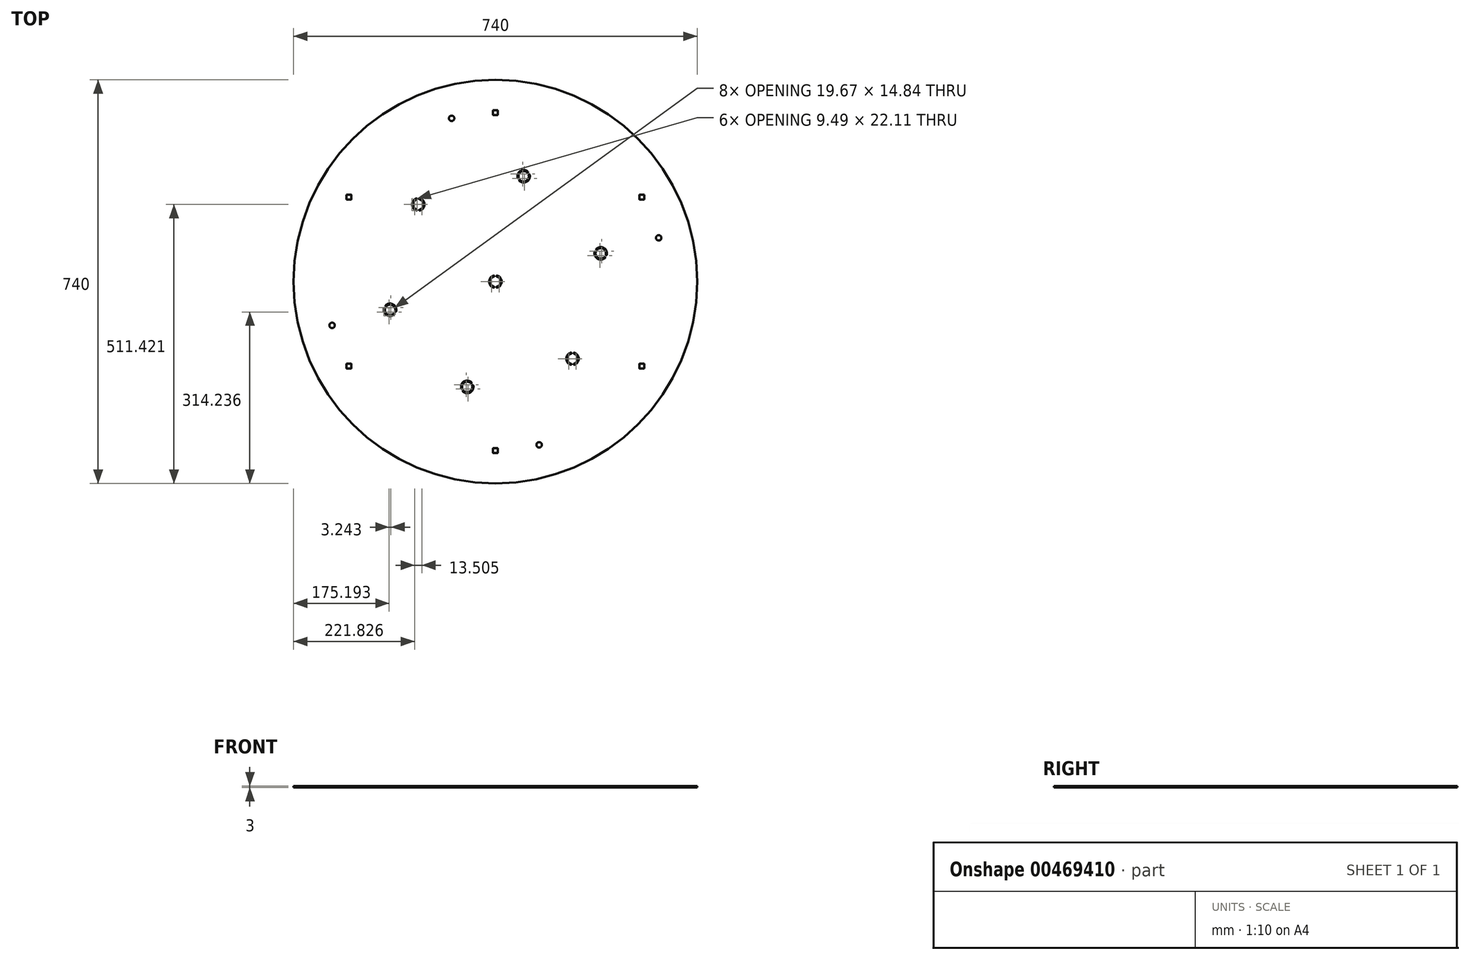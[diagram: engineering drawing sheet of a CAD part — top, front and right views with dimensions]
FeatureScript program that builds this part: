
annotation { "Feature Type Name" : "Feature", "Feature Type Description" : "" }
export const myFeature = defineFeature(function(context is Context, id is Id, definition is map)
    precondition{}
    {
        {
            var Q0;
            Q0=qCreatedBy(makeId("Top.planeOp"),FACE);
            var sketch = newSketch(context, id + "F0", { "sketchPlane" : qUnion([Q0])});
            skCircle(sketch, "E0", {"center": v(0, 0) * mm, "radius": 370 * mm});
            skSolve(sketch);
        }
        {
            var Q0;
            Q0=makeQuery(id+"F0.imprint","IMPRINT",FACE,{"disambiguationData":[TD([[makeQuery(id+"F0.imprint","IMPRINT",EDGE,{"derivedFrom":sQuery(id+"F0.wireOp",EDGE,"E0")}),1.0]])]});
            extrude(context, id + "F1", {"entities" : qUnion([Q0]), "depth" : 3 * mm});
        }
        {
            var Q0;
            Q0=makeQuery(id+"F1.opExtrude","CAP_FACE",FACE,{"disambiguationData":[OSD([sQuery(id+"F0.wireOp",EDGE,"E0")])],"isStart":false});
            var sketch = newSketch(context, id + "F2", { "sketchPlane" : qUnion([Q0])});
            skLineSegment(sketch, "E1", {"start": v(0, 310) * mm, "end": v(268.47, 155) * mm, "construction": true});
            skLineSegment(sketch, "E2", {"start": v(268.47, 155) * mm, "end": v(268.47, -155) * mm, "construction": true});
            skLineSegment(sketch, "E3", {"start": v(268.47, -155) * mm, "end": v(0, -310) * mm, "construction": true});
            skLineSegment(sketch, "E4", {"start": v(0, -310) * mm, "end": v(-268.47, -155) * mm, "construction": true});
            skLineSegment(sketch, "E5", {"start": v(-268.47, -155) * mm, "end": v(-268.47, 155) * mm, "construction": true});
            skLineSegment(sketch, "E6", {"start": v(-268.47, 155) * mm, "end": v(0, 310) * mm, "construction": true});
            skLineSegment(sketch, "E7.bottom", {"start": v(4, 314.5) * mm, "end": v(-4, 314.5) * mm});
            skLineSegment(sketch, "E7.top", {"start": v(4, 305.5) * mm, "end": v(-4, 305.5) * mm});
            skLineSegment(sketch, "E7.left", {"start": v(4.5, 314) * mm, "end": v(4.5, 306) * mm});
            skLineSegment(sketch, "E7.right", {"start": v(-4.5, 314) * mm, "end": v(-4.5, 306) * mm});
            skPoint(sketch, "E7.middle", {"position": v(0, 310) * mm});
            skLineSegment(sketch, "E8.bottom", {"start": v(272.47, 159.5) * mm, "end": v(264.47, 159.5) * mm});
            skLineSegment(sketch, "E8.top", {"start": v(272.47, 150.5) * mm, "end": v(264.47, 150.5) * mm});
            skLineSegment(sketch, "E8.left", {"start": v(272.97, 159) * mm, "end": v(272.97, 151) * mm});
            skLineSegment(sketch, "E8.right", {"start": v(263.97, 159) * mm, "end": v(263.97, 151) * mm});
            skPoint(sketch, "E8.middle", {"position": v(268.47, 155) * mm});
            skLineSegment(sketch, "E9.bottom", {"start": v(272.47, -150.5) * mm, "end": v(264.47, -150.5) * mm});
            skLineSegment(sketch, "E9.top", {"start": v(272.47, -159.5) * mm, "end": v(264.47, -159.5) * mm});
            skLineSegment(sketch, "E9.left", {"start": v(272.97, -151) * mm, "end": v(272.97, -159) * mm});
            skLineSegment(sketch, "E9.right", {"start": v(263.97, -151) * mm, "end": v(263.97, -159) * mm});
            skPoint(sketch, "E9.middle", {"position": v(268.47, -155) * mm});
            skLineSegment(sketch, "E10.bottom", {"start": v(-4, -305.5) * mm, "end": v(4, -305.5) * mm});
            skLineSegment(sketch, "E10.top", {"start": v(-4, -314.5) * mm, "end": v(4, -314.5) * mm});
            skLineSegment(sketch, "E10.left", {"start": v(-4.5, -306) * mm, "end": v(-4.5, -314) * mm});
            skLineSegment(sketch, "E10.right", {"start": v(4.5, -306) * mm, "end": v(4.5, -314) * mm});
            skPoint(sketch, "E10.middle", {"position": v(0, -310) * mm});
            skLineSegment(sketch, "E11.bottom", {"start": v(-264.47, -150.5) * mm, "end": v(-272.47, -150.5) * mm});
            skLineSegment(sketch, "E11.top", {"start": v(-264.47, -159.5) * mm, "end": v(-272.47, -159.5) * mm});
            skLineSegment(sketch, "E11.left", {"start": v(-263.97, -151) * mm, "end": v(-263.97, -159) * mm});
            skLineSegment(sketch, "E11.right", {"start": v(-272.97, -151) * mm, "end": v(-272.97, -159) * mm});
            skPoint(sketch, "E11.middle", {"position": v(-268.47, -155) * mm});
            skLineSegment(sketch, "E12.bottom", {"start": v(-264.47, 150.5) * mm, "end": v(-272.47, 150.5) * mm});
            skLineSegment(sketch, "E12.top", {"start": v(-264.47, 159.5) * mm, "end": v(-272.47, 159.5) * mm});
            skLineSegment(sketch, "E12.left", {"start": v(-263.97, 151) * mm, "end": v(-263.97, 159) * mm});
            skLineSegment(sketch, "E12.right", {"start": v(-272.97, 151) * mm, "end": v(-272.97, 159) * mm});
            skPoint(sketch, "E12.middle", {"position": v(-268.47, 155) * mm});
            skPoint(sketch, "E13.visualSharp", {"position": v(-4.5, 314.5) * mm});
            skArc(sketch, "E13.filletArc", {"start": v(-4, 314.5) * mm, "mid": v(-4.35, 314.35) * mm, "end": v(-4.5, 314) * mm});
            skPoint(sketch, "E14.visualSharp", {"position": v(4.5, 314.5) * mm});
            skArc(sketch, "E14.filletArc", {"start": v(4.5, 314) * mm, "mid": v(4.35, 314.35) * mm, "end": v(4, 314.5) * mm});
            skPoint(sketch, "E15.visualSharp", {"position": v(4.5, 305.5) * mm});
            skArc(sketch, "E15.filletArc", {"start": v(4, 305.5) * mm, "mid": v(4.35, 305.65) * mm, "end": v(4.5, 306) * mm});
            skPoint(sketch, "E16.visualSharp", {"position": v(-4.5, 305.5) * mm});
            skArc(sketch, "E16.filletArc", {"start": v(-4.5, 306) * mm, "mid": v(-4.35, 305.65) * mm, "end": v(-4, 305.5) * mm});
            skPoint(sketch, "E17.visualSharp", {"position": v(263.97, 159.5) * mm});
            skArc(sketch, "E17.filletArc", {"start": v(264.47, 159.5) * mm, "mid": v(264.11, 159.35) * mm, "end": v(263.97, 159) * mm});
            skPoint(sketch, "E18.visualSharp", {"position": v(272.97, 159.5) * mm});
            skArc(sketch, "E18.filletArc", {"start": v(272.97, 159) * mm, "mid": v(272.82, 159.35) * mm, "end": v(272.47, 159.5) * mm});
            skPoint(sketch, "E19.visualSharp", {"position": v(272.97, 150.5) * mm});
            skArc(sketch, "E19.filletArc", {"start": v(272.47, 150.5) * mm, "mid": v(272.82, 150.65) * mm, "end": v(272.97, 151) * mm});
            skPoint(sketch, "E20.visualSharp", {"position": v(263.97, 150.5) * mm});
            skArc(sketch, "E20.filletArc", {"start": v(263.97, 151) * mm, "mid": v(264.11, 150.65) * mm, "end": v(264.47, 150.5) * mm});
            skPoint(sketch, "E21.visualSharp", {"position": v(263.97, -150.5) * mm});
            skArc(sketch, "E21.filletArc", {"start": v(264.47, -150.5) * mm, "mid": v(264.11, -150.65) * mm, "end": v(263.97, -151) * mm});
            skPoint(sketch, "E22.visualSharp", {"position": v(272.97, -150.5) * mm});
            skArc(sketch, "E22.filletArc", {"start": v(272.97, -151) * mm, "mid": v(272.82, -150.65) * mm, "end": v(272.47, -150.5) * mm});
            skPoint(sketch, "E23.visualSharp", {"position": v(272.97, -159.5) * mm});
            skArc(sketch, "E23.filletArc", {"start": v(272.47, -159.5) * mm, "mid": v(272.82, -159.35) * mm, "end": v(272.97, -159) * mm});
            skPoint(sketch, "E24.visualSharp", {"position": v(263.97, -159.5) * mm});
            skArc(sketch, "E24.filletArc", {"start": v(263.97, -159) * mm, "mid": v(264.11, -159.35) * mm, "end": v(264.47, -159.5) * mm});
            skPoint(sketch, "E25.visualSharp", {"position": v(-4.5, -305.5) * mm});
            skArc(sketch, "E25.filletArc", {"start": v(-4, -305.5) * mm, "mid": v(-4.35, -305.65) * mm, "end": v(-4.5, -306) * mm});
            skPoint(sketch, "E26.visualSharp", {"position": v(4.5, -305.5) * mm});
            skArc(sketch, "E26.filletArc", {"start": v(4.5, -306) * mm, "mid": v(4.35, -305.65) * mm, "end": v(4, -305.5) * mm});
            skPoint(sketch, "E27.visualSharp", {"position": v(4.5, -314.5) * mm});
            skArc(sketch, "E27.filletArc", {"start": v(4, -314.5) * mm, "mid": v(4.35, -314.35) * mm, "end": v(4.5, -314) * mm});
            skPoint(sketch, "E28.visualSharp", {"position": v(-4.5, -314.5) * mm});
            skArc(sketch, "E28.filletArc", {"start": v(-4.5, -314) * mm, "mid": v(-4.35, -314.35) * mm, "end": v(-4, -314.5) * mm});
            skPoint(sketch, "E29.visualSharp", {"position": v(-272.97, -159.5) * mm});
            skArc(sketch, "E29.filletArc", {"start": v(-272.97, -159) * mm, "mid": v(-272.82, -159.35) * mm, "end": v(-272.47, -159.5) * mm});
            skPoint(sketch, "E30.visualSharp", {"position": v(-272.97, -150.5) * mm});
            skArc(sketch, "E30.filletArc", {"start": v(-272.47, -150.5) * mm, "mid": v(-272.82, -150.65) * mm, "end": v(-272.97, -151) * mm});
            skPoint(sketch, "E31.visualSharp", {"position": v(-263.97, -150.5) * mm});
            skArc(sketch, "E31.filletArc", {"start": v(-263.97, -151) * mm, "mid": v(-264.11, -150.65) * mm, "end": v(-264.47, -150.5) * mm});
            skPoint(sketch, "E32.visualSharp", {"position": v(-263.97, -159.5) * mm});
            skArc(sketch, "E32.filletArc", {"start": v(-264.47, -159.5) * mm, "mid": v(-264.11, -159.35) * mm, "end": v(-263.97, -159) * mm});
            skPoint(sketch, "E33.visualSharp", {"position": v(-263.97, 150.5) * mm});
            skArc(sketch, "E33.filletArc", {"start": v(-264.47, 150.5) * mm, "mid": v(-264.11, 150.65) * mm, "end": v(-263.97, 151) * mm});
            skPoint(sketch, "E34.visualSharp", {"position": v(-263.97, 159.5) * mm});
            skArc(sketch, "E34.filletArc", {"start": v(-263.97, 159) * mm, "mid": v(-264.11, 159.35) * mm, "end": v(-264.47, 159.5) * mm});
            skPoint(sketch, "E35.visualSharp", {"position": v(-272.97, 159.5) * mm});
            skArc(sketch, "E35.filletArc", {"start": v(-272.47, 159.5) * mm, "mid": v(-272.82, 159.35) * mm, "end": v(-272.97, 159) * mm});
            skPoint(sketch, "E36.visualSharp", {"position": v(-272.97, 150.5) * mm});
            skArc(sketch, "E36.filletArc", {"start": v(-272.97, 151) * mm, "mid": v(-272.82, 150.65) * mm, "end": v(-272.47, 150.5) * mm});
            skSolve(sketch);
        }
        {
            var Q0;
            Q0 = qSketchRegion(id + "F2", true);
            extrude(context, id + "F3", {"entities" : qUnion([Q0]), "operationType" : NewBodyOperationType.REMOVE, "oppositeDirection" : true, "depth" : 5 * mm});
        }
        {
            var Q0;
            Q0=makeQuery(id+"F1.opExtrude","CAP_FACE",FACE,{"disambiguationData":[OSD([sQuery(id+"F0.wireOp",EDGE,"E0")])],"isStart":false});
            var sketch = newSketch(context, id + "F4", { "sketchPlane" : qUnion([Q0])});
            skArc(sketch, "E37", {"start": v(3.29, -11.02) * mm, "mid": v(11.5, 0) * mm, "end": v(3.29, 11.02) * mm});
            skArc(sketch, "E38", {"start": v(2.71, -9.1) * mm, "mid": v(9.5, 0) * mm, "end": v(2.71, 9.1) * mm});
            skLineSegment(sketch, "E39.left", {"start": v(-2, -10.06) * mm, "end": v(-2, -10.06) * mm});
            skLineSegment(sketch, "E39.right", {"start": v(2, -10.06) * mm, "end": v(2, -10.06) * mm});
            skLineSegment(sketch, "E40.trimOffspring", {"start": v(2, 10.06) * mm, "end": v(2, 10.06) * mm});
            skLineSegment(sketch, "E41.trimOffspring", {"start": v(-2, 10.06) * mm, "end": v(-2, 10.06) * mm});
            skArc(sketch, "E42.trimOffspring", {"start": v(-2.71, 9.1) * mm, "mid": v(-9.5, 0) * mm, "end": v(-2.71, -9.1) * mm});
            skArc(sketch, "E43.trimOffspring", {"start": v(-3.29, 11.02) * mm, "mid": v(-11.5, 0) * mm, "end": v(-3.29, -11.02) * mm});
            skPoint(sketch, "E44.visualSharp", {"position": v(-2, -11.32) * mm});
            skArc(sketch, "E44.filletArc", {"start": v(-3.29, -11.02) * mm, "mid": v(-2.4, -10.86) * mm, "end": v(-2, -10.06) * mm});
            skPoint(sketch, "E45.visualSharp", {"position": v(-2, -9.29) * mm});
            skArc(sketch, "E45.filletArc", {"start": v(-2, -10.06) * mm, "mid": v(-2.2, -9.46) * mm, "end": v(-2.71, -9.1) * mm});
            skPoint(sketch, "E46.visualSharp", {"position": v(2, -9.29) * mm});
            skArc(sketch, "E46.filletArc", {"start": v(2.71, -9.1) * mm, "mid": v(2.2, -9.46) * mm, "end": v(2, -10.06) * mm});
            skPoint(sketch, "E47.visualSharp", {"position": v(2, -11.32) * mm});
            skArc(sketch, "E47.filletArc", {"start": v(2, -10.06) * mm, "mid": v(2.4, -10.86) * mm, "end": v(3.29, -11.02) * mm});
            skPoint(sketch, "E48.visualSharp", {"position": v(-2, 9.29) * mm});
            skArc(sketch, "E48.filletArc", {"start": v(-2.71, 9.1) * mm, "mid": v(-2.2, 9.46) * mm, "end": v(-2, 10.06) * mm});
            skPoint(sketch, "E49.visualSharp", {"position": v(-2, 11.32) * mm});
            skArc(sketch, "E49.filletArc", {"start": v(-2, 10.06) * mm, "mid": v(-2.4, 10.86) * mm, "end": v(-3.29, 11.02) * mm});
            skPoint(sketch, "E50.visualSharp", {"position": v(2, 9.29) * mm});
            skArc(sketch, "E50.filletArc", {"start": v(2, 10.06) * mm, "mid": v(2.2, 9.46) * mm, "end": v(2.71, 9.1) * mm});
            skPoint(sketch, "E51.visualSharp", {"position": v(2, 11.32) * mm});
            skArc(sketch, "E51.filletArc", {"start": v(3.29, 11.02) * mm, "mid": v(2.4, 10.86) * mm, "end": v(2, 10.06) * mm});
            skSolve(sketch);
        }
        {
            var Q0;
            Q0=makeQuery(id+"F4.imprint","IMPRINT",FACE,{"disambiguationData":[TD([[makeQuery(id+"F4.imprint","IMPRINT",EDGE,{"derivedFrom":sQuery(id+"F4.wireOp",EDGE,"E37")}),-1.0]])]});
            extrude(context, id + "F5", {"entities" : qUnion([Q0]), "operationType" : NewBodyOperationType.INTERSECT, "endBound" : BoundingType.UP_TO_NEXT, "oppositeDirection" : true, "depth" : 3 * mm});
        }
        {
            var Q0;
            Q0=makeQuery(id+"F1.opExtrude","CAP_FACE",FACE,{"disambiguationData":[OSD([sQuery(id+"F0.wireOp",EDGE,"E0")])],"isStart":false});
            var sketch = newSketch(context, id + "F6", { "sketchPlane" : qUnion([Q0])});
            skLineSegment(sketch, "E52", {"start": v(80.23, -299.44) * mm, "end": v(-299.44, -80.23) * mm, "construction": true});
            skLineSegment(sketch, "E53", {"start": v(-299.44, -80.23) * mm, "end": v(-80.23, 299.44) * mm, "construction": true});
            skLineSegment(sketch, "E54", {"start": v(-80.23, 299.44) * mm, "end": v(299.44, 80.23) * mm, "construction": true});
            skLineSegment(sketch, "E55", {"start": v(299.44, 80.23) * mm, "end": v(80.23, -299.44) * mm, "construction": true});
            skLineSegment(sketch, "E56", {"start": v(-299.44, -80.23) * mm, "end": v(299.44, 80.23) * mm, "construction": true});
            skLineSegment(sketch, "E57", {"start": v(-80.23, 299.44) * mm, "end": v(80.23, -299.44) * mm, "construction": true});
            skCircle(sketch, "E58", {"center": v(-80.23, 299.44) * mm, "radius": 5 * mm});
            skCircle(sketch, "E59", {"center": v(299.44, 80.23) * mm, "radius": 5 * mm});
            skCircle(sketch, "E60", {"center": v(80.23, -299.44) * mm, "radius": 5 * mm});
            skCircle(sketch, "E61", {"center": v(-299.44, -80.23) * mm, "radius": 5 * mm});
            skSolve(sketch);
        }
        {
            var Q0;
            Q0=makeQuery(id+"F6.imprint","IMPRINT",FACE,{"disambiguationData":[TD([[makeQuery(id+"F6.imprint","IMPRINT",EDGE,{"derivedFrom":sQuery(id+"F6.wireOp",EDGE,"E58")}),-1.0]])]});
            extrude(context, id + "F7", {"entities" : qUnion([Q0]), "operationType" : NewBodyOperationType.INTERSECT, "oppositeDirection" : true, "depth" : 3 * mm});
        }
        {
            var Q0;
            Q0=makeQuery(id+"F1.opExtrude","CAP_FACE",FACE,{"disambiguationData":[OSD([sQuery(id+"F0.wireOp",EDGE,"E0")])],"isStart":false});
            var sketch = newSketch(context, id + "F8", { "sketchPlane" : qUnion([Q0])});
            skArc(sketch, "E62", {"start": v(-138.14, 130.4) * mm, "mid": v(-129.92, 141.42) * mm, "end": v(-138.14, 152.44) * mm});
            skArc(sketch, "E63", {"start": v(-138.7, 132.32) * mm, "mid": v(-131.92, 141.42) * mm, "end": v(-138.7, 150.53) * mm});
            skLineSegment(sketch, "E64.left", {"start": v(-143.42, 151.48) * mm, "end": v(-143.42, 151.48) * mm});
            skLineSegment(sketch, "E64.right", {"start": v(-139.42, 151.48) * mm, "end": v(-139.42, 151.48) * mm});
            skLineSegment(sketch, "E65.trimOffspring", {"start": v(-139.42, 131.36) * mm, "end": v(-139.42, 131.36) * mm});
            skLineSegment(sketch, "E66.trimOffspring", {"start": v(-143.42, 131.36) * mm, "end": v(-143.42, 131.36) * mm});
            skArc(sketch, "E67.trimOffspring", {"start": v(-144.14, 150.53) * mm, "mid": v(-150.92, 141.42) * mm, "end": v(-144.14, 132.32) * mm});
            skArc(sketch, "E68.trimOffspring", {"start": v(-144.7, 152.44) * mm, "mid": v(-152.92, 141.42) * mm, "end": v(-144.7, 130.4) * mm});
            skPoint(sketch, "E69.visualSharp", {"position": v(-143.42, 150.7) * mm});
            skArc(sketch, "E69.filletArc", {"start": v(-144.14, 150.53) * mm, "mid": v(-143.62, 150.89) * mm, "end": v(-143.42, 151.48) * mm});
            skPoint(sketch, "E70.visualSharp", {"position": v(-143.42, 152.75) * mm});
            skArc(sketch, "E70.filletArc", {"start": v(-143.42, 151.48) * mm, "mid": v(-143.82, 152.29) * mm, "end": v(-144.7, 152.44) * mm});
            skPoint(sketch, "E71.visualSharp", {"position": v(-139.42, 150.7) * mm});
            skArc(sketch, "E71.filletArc", {"start": v(-139.42, 151.48) * mm, "mid": v(-139.22, 150.89) * mm, "end": v(-138.7, 150.53) * mm});
            skPoint(sketch, "E72.visualSharp", {"position": v(-139.42, 152.75) * mm});
            skArc(sketch, "E72.filletArc", {"start": v(-138.14, 152.44) * mm, "mid": v(-139.02, 152.29) * mm, "end": v(-139.42, 151.48) * mm});
            skPoint(sketch, "E73.visualSharp", {"position": v(-143.42, 132.13) * mm});
            skArc(sketch, "E73.filletArc", {"start": v(-143.42, 131.36) * mm, "mid": v(-143.62, 131.96) * mm, "end": v(-144.14, 132.32) * mm});
            skPoint(sketch, "E74.visualSharp", {"position": v(-143.42, 130.1) * mm});
            skArc(sketch, "E74.filletArc", {"start": v(-144.7, 130.4) * mm, "mid": v(-143.82, 130.56) * mm, "end": v(-143.42, 131.36) * mm});
            skPoint(sketch, "E75.visualSharp", {"position": v(-139.42, 130.1) * mm});
            skArc(sketch, "E75.filletArc", {"start": v(-139.42, 131.36) * mm, "mid": v(-139.02, 130.56) * mm, "end": v(-138.14, 130.4) * mm});
            skPoint(sketch, "E76.visualSharp", {"position": v(-139.42, 132.13) * mm});
            skArc(sketch, "E76.filletArc", {"start": v(-138.7, 132.32) * mm, "mid": v(-139.22, 131.96) * mm, "end": v(-139.42, 131.36) * mm});
            skLineSegment(sketch, "E77", {"start": v(-141.42, 141.42) * mm, "end": v(0, 0) * mm, "construction": true});
            skPoint(sketch, "E78.1.0", {"position": v(-184.38, -59.16) * mm});
            skPoint(sketch, "E78.1.1", {"position": v(-200.23, -45.39) * mm});
            skPoint(sketch, "E78.1.2", {"position": v(-204, -47.83) * mm});
            skArc(sketch, "E78.1.3", {"start": v(-204.37, -49.1) * mm, "mid": v(-198.94, -61.72) * mm, "end": v(-185.28, -60.12) * mm});
            skArc(sketch, "E78.1.4", {"start": v(-202.43, -49.56) * mm, "mid": v(-197.94, -60) * mm, "end": v(-186.66, -58.67) * mm});
            skArc(sketch, "E78.1.5", {"start": v(-183.94, -53.97) * mm, "mid": v(-188.44, -43.54) * mm, "end": v(-199.71, -44.86) * mm});
            skArc(sketch, "E78.1.6", {"start": v(-182, -54.43) * mm, "mid": v(-187.44, -41.8) * mm, "end": v(-201.09, -43.4) * mm});
            skPoint(sketch, "E78.1.7", {"position": v(-186.14, -58.14) * mm});
            skPoint(sketch, "E78.1.8", {"position": v(-202.23, -48.85) * mm});
            skPoint(sketch, "E78.1.9", {"position": v(-184.14, -54.68) * mm});
            skPoint(sketch, "E78.1.10", {"position": v(-202, -44.37) * mm});
            skPoint(sketch, "E78.1.11", {"position": v(-182.38, -55.7) * mm});
            skArc(sketch, "E78.1.12", {"start": v(-183.94, -53.97) * mm, "mid": v(-183.89, -54.6) * mm, "end": v(-183.47, -55.06) * mm});
            skArc(sketch, "E78.1.13", {"start": v(-183.47, -55.06) * mm, "mid": v(-182.58, -55.12) * mm, "end": v(-182, -54.43) * mm});
            skArc(sketch, "E78.1.14", {"start": v(-185.28, -60.12) * mm, "mid": v(-184.98, -59.28) * mm, "end": v(-185.47, -58.53) * mm});
            skArc(sketch, "E78.1.15", {"start": v(-185.47, -58.53) * mm, "mid": v(-186.09, -58.4) * mm, "end": v(-186.66, -58.67) * mm});
            skArc(sketch, "E78.1.16", {"start": v(-201.09, -43.4) * mm, "mid": v(-201.4, -44.25) * mm, "end": v(-200.9, -45) * mm});
            skArc(sketch, "E78.1.17", {"start": v(-200.9, -45) * mm, "mid": v(-200.28, -45.13) * mm, "end": v(-199.71, -44.86) * mm});
            skArc(sketch, "E78.1.18", {"start": v(-202.9, -48.46) * mm, "mid": v(-203.8, -48.41) * mm, "end": v(-204.37, -49.1) * mm});
            skArc(sketch, "E78.1.19", {"start": v(-202.43, -49.56) * mm, "mid": v(-202.48, -48.94) * mm, "end": v(-202.9, -48.46) * mm});
            skPoint(sketch, "E78.2.0", {"position": v(-40.96, -189.25) * mm});
            skPoint(sketch, "E78.2.1", {"position": v(-60.8, -196.1) * mm});
            skPoint(sketch, "E78.2.2", {"position": v(-60.57, -200.58) * mm});
            skArc(sketch, "E78.2.3", {"start": v(-59.67, -201.54) * mm, "mid": v(-46.01, -203.14) * mm, "end": v(-40.58, -190.52) * mm});
            skArc(sketch, "E78.2.4", {"start": v(-58.3, -200.09) * mm, "mid": v(-47.01, -201.41) * mm, "end": v(-42.52, -190.98) * mm});
            skArc(sketch, "E78.2.5", {"start": v(-45.24, -186.28) * mm, "mid": v(-56.51, -184.96) * mm, "end": v(-61, -195.39) * mm});
            skArc(sketch, "E78.2.6", {"start": v(-43.86, -184.83) * mm, "mid": v(-57.51, -183.23) * mm, "end": v(-62.95, -195.85) * mm});
            skPoint(sketch, "E78.2.7", {"position": v(-42.72, -190.27) * mm});
            skPoint(sketch, "E78.2.8", {"position": v(-58.8, -199.56) * mm});
            skPoint(sketch, "E78.2.9", {"position": v(-44.72, -186.8) * mm});
            skPoint(sketch, "E78.2.10", {"position": v(-62.57, -197.12) * mm});
            skPoint(sketch, "E78.2.11", {"position": v(-42.96, -185.8) * mm});
            skArc(sketch, "E78.2.12", {"start": v(-45.24, -186.28) * mm, "mid": v(-44.67, -186.55) * mm, "end": v(-44.05, -186.42) * mm});
            skArc(sketch, "E78.2.13", {"start": v(-44.05, -186.42) * mm, "mid": v(-43.56, -185.67) * mm, "end": v(-43.86, -184.83) * mm});
            skArc(sketch, "E78.2.14", {"start": v(-40.58, -190.52) * mm, "mid": v(-41.15, -189.83) * mm, "end": v(-42.05, -189.89) * mm});
            skArc(sketch, "E78.2.15", {"start": v(-42.05, -189.89) * mm, "mid": v(-42.47, -190.36) * mm, "end": v(-42.52, -190.98) * mm});
            skArc(sketch, "E78.2.16", {"start": v(-62.95, -195.85) * mm, "mid": v(-62.37, -196.54) * mm, "end": v(-61.48, -196.48) * mm});
            skArc(sketch, "E78.2.17", {"start": v(-61.48, -196.48) * mm, "mid": v(-61.06, -196.01) * mm, "end": v(-61, -195.39) * mm});
            skArc(sketch, "E78.2.18", {"start": v(-59.48, -199.95) * mm, "mid": v(-59.97, -200.7) * mm, "end": v(-59.67, -201.54) * mm});
            skArc(sketch, "E78.2.19", {"start": v(-58.3, -200.09) * mm, "mid": v(-58.86, -199.82) * mm, "end": v(-59.48, -199.95) * mm});
            skPoint(sketch, "E78.3.0", {"position": v(143.42, -130.1) * mm});
            skPoint(sketch, "E78.3.1", {"position": v(139.42, -150.7) * mm});
            skPoint(sketch, "E78.3.2", {"position": v(143.42, -152.75) * mm});
            skArc(sketch, "E78.3.3", {"start": v(144.7, -152.44) * mm, "mid": v(152.92, -141.42) * mm, "end": v(144.7, -130.4) * mm});
            skArc(sketch, "E78.3.4", {"start": v(144.14, -150.53) * mm, "mid": v(150.92, -141.42) * mm, "end": v(144.14, -132.32) * mm});
            skArc(sketch, "E78.3.5", {"start": v(138.7, -132.32) * mm, "mid": v(131.92, -141.42) * mm, "end": v(138.7, -150.53) * mm});
            skArc(sketch, "E78.3.6", {"start": v(138.14, -130.4) * mm, "mid": v(129.92, -141.42) * mm, "end": v(138.14, -152.44) * mm});
            skPoint(sketch, "E78.3.7", {"position": v(143.42, -132.13) * mm});
            skPoint(sketch, "E78.3.8", {"position": v(143.42, -150.7) * mm});
            skPoint(sketch, "E78.3.9", {"position": v(139.42, -132.13) * mm});
            skPoint(sketch, "E78.3.10", {"position": v(139.42, -152.75) * mm});
            skPoint(sketch, "E78.3.11", {"position": v(139.42, -130.1) * mm});
            skArc(sketch, "E78.3.12", {"start": v(138.7, -132.32) * mm, "mid": v(139.22, -131.96) * mm, "end": v(139.42, -131.36) * mm});
            skArc(sketch, "E78.3.13", {"start": v(139.42, -131.36) * mm, "mid": v(139.02, -130.56) * mm, "end": v(138.14, -130.4) * mm});
            skArc(sketch, "E78.3.14", {"start": v(144.7, -130.4) * mm, "mid": v(143.82, -130.56) * mm, "end": v(143.42, -131.36) * mm});
            skArc(sketch, "E78.3.15", {"start": v(143.42, -131.36) * mm, "mid": v(143.62, -131.96) * mm, "end": v(144.14, -132.32) * mm});
            skArc(sketch, "E78.3.16", {"start": v(138.14, -152.44) * mm, "mid": v(139.02, -152.29) * mm, "end": v(139.42, -151.48) * mm});
            skArc(sketch, "E78.3.17", {"start": v(139.42, -151.48) * mm, "mid": v(139.22, -150.89) * mm, "end": v(138.7, -150.53) * mm});
            skArc(sketch, "E78.3.18", {"start": v(143.42, -151.48) * mm, "mid": v(143.82, -152.29) * mm, "end": v(144.7, -152.44) * mm});
            skArc(sketch, "E78.3.19", {"start": v(144.14, -150.53) * mm, "mid": v(143.62, -150.89) * mm, "end": v(143.42, -151.48) * mm});
            skPoint(sketch, "E78.4.0", {"position": v(184.38, 59.16) * mm});
            skPoint(sketch, "E78.4.1", {"position": v(200.23, 45.39) * mm});
            skPoint(sketch, "E78.4.2", {"position": v(204, 47.83) * mm});
            skArc(sketch, "E78.4.3", {"start": v(204.37, 49.1) * mm, "mid": v(198.94, 61.72) * mm, "end": v(185.28, 60.12) * mm});
            skArc(sketch, "E78.4.4", {"start": v(202.43, 49.56) * mm, "mid": v(197.94, 60) * mm, "end": v(186.66, 58.67) * mm});
            skArc(sketch, "E78.4.5", {"start": v(183.94, 53.97) * mm, "mid": v(188.44, 43.54) * mm, "end": v(199.71, 44.86) * mm});
            skArc(sketch, "E78.4.6", {"start": v(182, 54.43) * mm, "mid": v(187.44, 41.8) * mm, "end": v(201.09, 43.4) * mm});
            skPoint(sketch, "E78.4.7", {"position": v(186.14, 58.14) * mm});
            skPoint(sketch, "E78.4.8", {"position": v(202.23, 48.85) * mm});
            skPoint(sketch, "E78.4.9", {"position": v(184.14, 54.68) * mm});
            skPoint(sketch, "E78.4.10", {"position": v(202, 44.37) * mm});
            skPoint(sketch, "E78.4.11", {"position": v(182.38, 55.7) * mm});
            skArc(sketch, "E78.4.12", {"start": v(183.94, 53.97) * mm, "mid": v(183.89, 54.6) * mm, "end": v(183.47, 55.06) * mm});
            skArc(sketch, "E78.4.13", {"start": v(183.47, 55.06) * mm, "mid": v(182.58, 55.12) * mm, "end": v(182, 54.43) * mm});
            skArc(sketch, "E78.4.14", {"start": v(185.28, 60.12) * mm, "mid": v(184.98, 59.28) * mm, "end": v(185.47, 58.53) * mm});
            skArc(sketch, "E78.4.15", {"start": v(185.47, 58.53) * mm, "mid": v(186.09, 58.4) * mm, "end": v(186.66, 58.67) * mm});
            skArc(sketch, "E78.4.16", {"start": v(201.09, 43.4) * mm, "mid": v(201.4, 44.25) * mm, "end": v(200.9, 45) * mm});
            skArc(sketch, "E78.4.17", {"start": v(200.9, 45) * mm, "mid": v(200.28, 45.13) * mm, "end": v(199.71, 44.86) * mm});
            skArc(sketch, "E78.4.18", {"start": v(202.9, 48.46) * mm, "mid": v(203.8, 48.41) * mm, "end": v(204.37, 49.1) * mm});
            skArc(sketch, "E78.4.19", {"start": v(202.43, 49.56) * mm, "mid": v(202.48, 48.94) * mm, "end": v(202.9, 48.46) * mm});
            skPoint(sketch, "E78.5.0", {"position": v(40.96, 189.25) * mm});
            skPoint(sketch, "E78.5.1", {"position": v(60.8, 196.1) * mm});
            skPoint(sketch, "E78.5.2", {"position": v(60.57, 200.58) * mm});
            skArc(sketch, "E78.5.3", {"start": v(59.67, 201.54) * mm, "mid": v(46.01, 203.14) * mm, "end": v(40.58, 190.52) * mm});
            skArc(sketch, "E78.5.4", {"start": v(58.3, 200.09) * mm, "mid": v(47.01, 201.41) * mm, "end": v(42.52, 190.98) * mm});
            skArc(sketch, "E78.5.5", {"start": v(45.24, 186.28) * mm, "mid": v(56.51, 184.96) * mm, "end": v(61, 195.39) * mm});
            skArc(sketch, "E78.5.6", {"start": v(43.86, 184.83) * mm, "mid": v(57.51, 183.23) * mm, "end": v(62.95, 195.85) * mm});
            skPoint(sketch, "E78.5.7", {"position": v(42.72, 190.27) * mm});
            skPoint(sketch, "E78.5.8", {"position": v(58.8, 199.56) * mm});
            skPoint(sketch, "E78.5.9", {"position": v(44.72, 186.8) * mm});
            skPoint(sketch, "E78.5.10", {"position": v(62.57, 197.12) * mm});
            skPoint(sketch, "E78.5.11", {"position": v(42.96, 185.8) * mm});
            skArc(sketch, "E78.5.12", {"start": v(45.24, 186.28) * mm, "mid": v(44.67, 186.55) * mm, "end": v(44.05, 186.42) * mm});
            skArc(sketch, "E78.5.13", {"start": v(44.05, 186.42) * mm, "mid": v(43.56, 185.67) * mm, "end": v(43.86, 184.83) * mm});
            skArc(sketch, "E78.5.14", {"start": v(40.58, 190.52) * mm, "mid": v(41.15, 189.83) * mm, "end": v(42.05, 189.89) * mm});
            skArc(sketch, "E78.5.15", {"start": v(42.05, 189.89) * mm, "mid": v(42.47, 190.36) * mm, "end": v(42.52, 190.98) * mm});
            skArc(sketch, "E78.5.16", {"start": v(62.95, 195.85) * mm, "mid": v(62.37, 196.54) * mm, "end": v(61.48, 196.48) * mm});
            skArc(sketch, "E78.5.17", {"start": v(61.48, 196.48) * mm, "mid": v(61.06, 196.01) * mm, "end": v(61, 195.39) * mm});
            skArc(sketch, "E78.5.18", {"start": v(59.48, 199.95) * mm, "mid": v(59.97, 200.7) * mm, "end": v(59.67, 201.54) * mm});
            skArc(sketch, "E78.5.19", {"start": v(58.3, 200.09) * mm, "mid": v(58.86, 199.82) * mm, "end": v(59.48, 199.95) * mm});
            skPoint(sketch, "E78.center", {"position": v(0, 0) * mm});
            skSolve(sketch);
        }
        {
            var Q0;
            Q0=makeQuery(id+"F8.imprint","IMPRINT",FACE,{"disambiguationData":[TD([[makeQuery(id+"F8.imprint","IMPRINT",EDGE,{"derivedFrom":sQuery(id+"F8.wireOp",EDGE,"E62")}),-1.0]])]});
            extrude(context, id + "F9", {"entities" : qUnion([Q0]), "operationType" : NewBodyOperationType.INTERSECT, "endBound" : BoundingType.UP_TO_NEXT, "oppositeDirection" : true, "depth" : 25 * mm});
        }
    });
